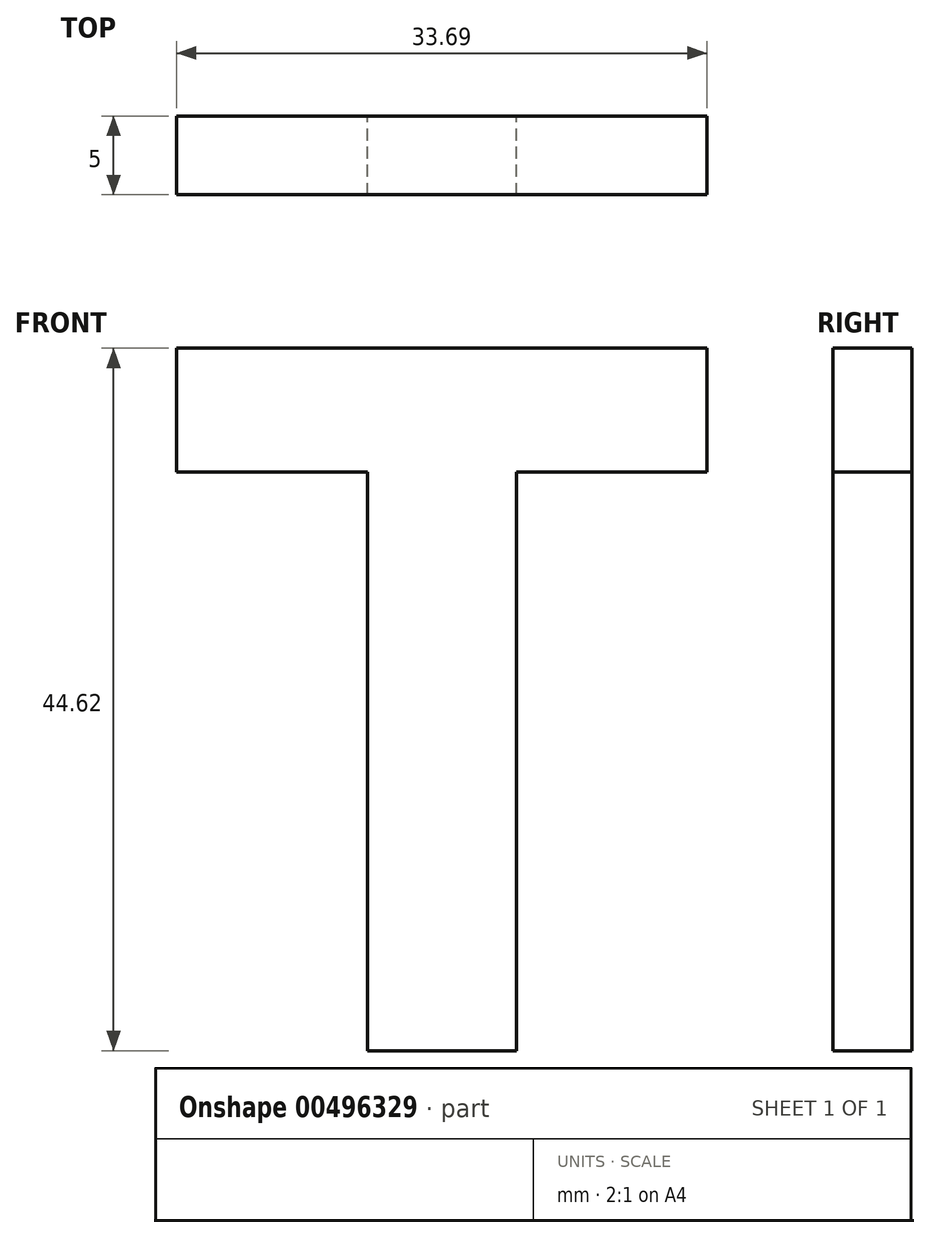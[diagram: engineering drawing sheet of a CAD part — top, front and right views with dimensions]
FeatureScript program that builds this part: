
annotation { "Feature Type Name" : "Feature", "Feature Type Description" : "" }
export const myFeature = defineFeature(function(context is Context, id is Id, definition is map)
    precondition{}
    {
        {
            var Q0;
            Q0=qCreatedBy(makeId("Front.planeOp"),FACE);
            var sketch = newSketch(context, id + "F0", { "sketchPlane" : qUnion([Q0])});
            skText(sketch, "E0", { "text": "T", "fontName": "OpenSans-Bold.ttf"});
            const initialGuessF0  = {"E0": [-0.06157, 0.01573, 1, 0, 0.045]};
            skSetInitialGuess(sketch, initialGuessF0);
            skSolve(sketch);
        }
        {
            var Q0;
            Q0=makeQuery(id+"F0.imprint","IMPRINT",FACE,{"disambiguationData":[TD([[makeQuery(id+"F0.imprint","IMPRINT",EDGE,{"derivedFrom":sQuery(id+"F0.wireOp",EDGE,"E0.sketch_text.stroke-0")}),-1.0]])]});
            extrude(context, id + "F1", {"entities" : qUnion([Q0]), "depth" : 5 * mm});
        }
    });
